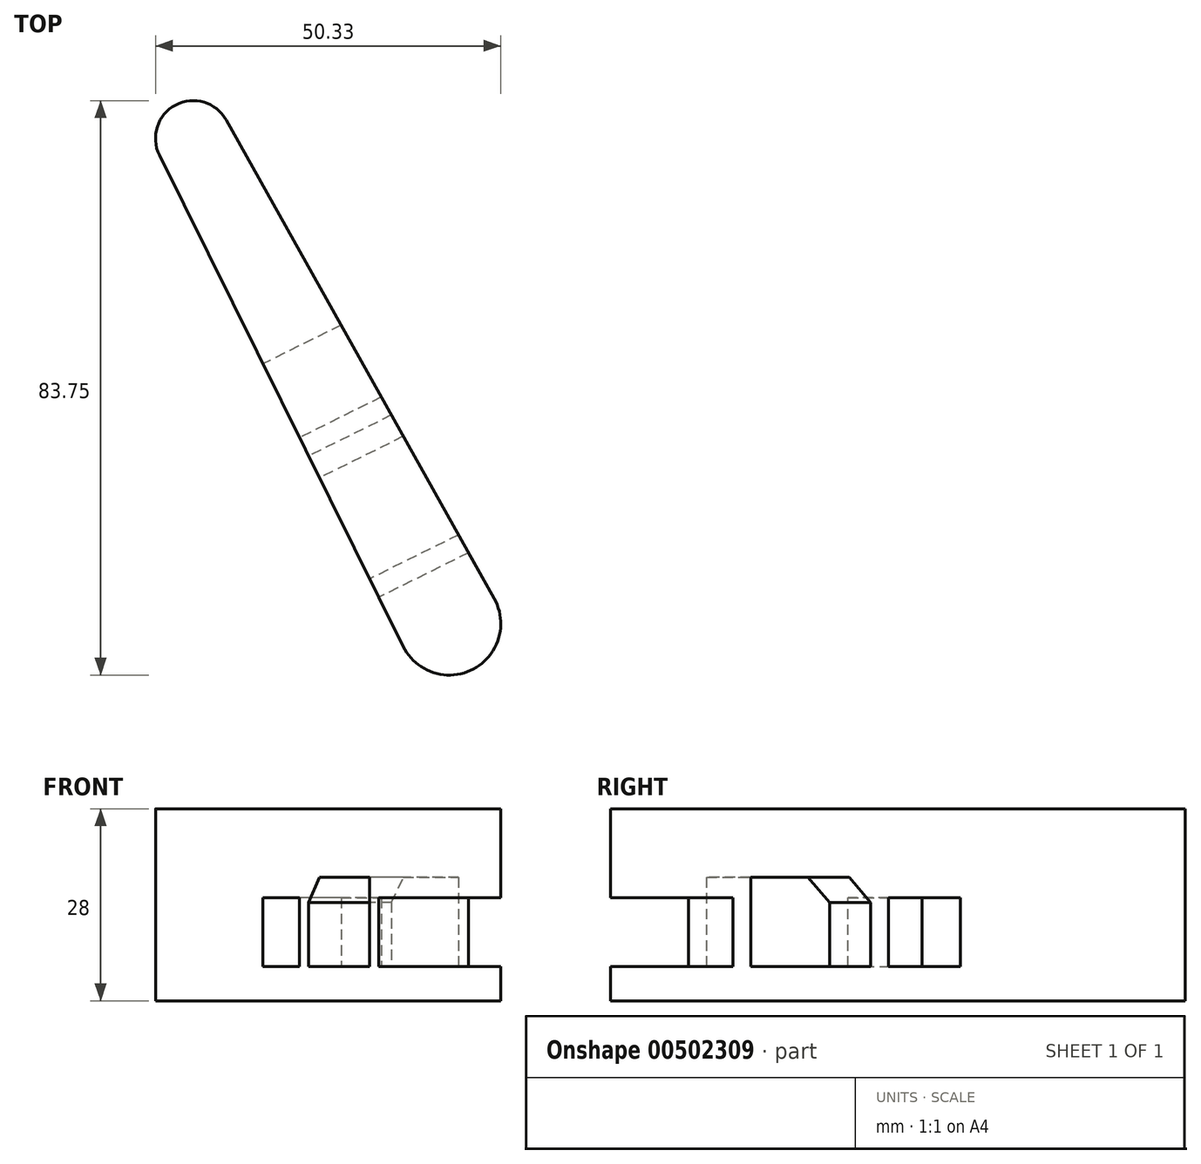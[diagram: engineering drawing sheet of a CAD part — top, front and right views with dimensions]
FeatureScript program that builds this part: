
annotation { "Feature Type Name" : "Feature", "Feature Type Description" : "" }
export const myFeature = defineFeature(function(context is Context, id is Id, definition is map)
    precondition{}
    {
        {
            var Q0;
            Q0=qCreatedBy(makeId("Top.planeOp"),FACE);
            var sketch = newSketch(context, id + "F0", { "sketchPlane" : qUnion([Q0])});
            skCircle(sketch, "E0", {"center": v(-17.98, -33.67) * mm, "radius": 7.5 * mm});
            skLineSegment(sketch, "E1", {"start": v(-17.98, -33.67) * mm, "end": v(-55.31, 37.08) * mm});
            skCircle(sketch, "E2", {"center": v(-55.31, 37.08) * mm, "radius": 5.5 * mm});
            skLineSegment(sketch, "E3", {"start": v(-50.52, 39.8) * mm, "end": v(-11.44, -30) * mm});
            skLineSegment(sketch, "E4", {"start": v(-11.44, -30) * mm, "end": v(-24.7, -37) * mm});
            skLineSegment(sketch, "E5", {"start": v(-24.7, -37) * mm, "end": v(-60.24, 34.64) * mm});
            skSolve(sketch);
        }
        {
            var Q0;
            Q0 = qSketchRegion(id + "F0", true);
            extrude(context, id + "F1", {"entities" : qUnion([Q0]), "depth" : 28 * mm});
        }
        {
            var Q0;
            Q0=makeQuery(id+"F1.opExtrude","SWEPT_FACE",FACE,{"disambiguationData":[OSD([sQuery(id+"F0.wireOp",EDGE,"E5")])]});
            var sketch = newSketch(context, id + "F2", { "sketchPlane" : qUnion([Q0])});
            skLineSegment(sketch, "E6", {"start": v(22.18, 0) * mm, "end": v(22.18, 5) * mm});
            skLineSegment(sketch, "E7.bottom", {"start": v(22.18, 5) * mm, "end": v(14.18, 5) * mm});
            skLineSegment(sketch, "E7.top", {"start": v(22.18, 15) * mm, "end": v(14.18, 15) * mm});
            skLineSegment(sketch, "E7.left", {"start": v(22.18, 5) * mm, "end": v(22.18, 15) * mm});
            skLineSegment(sketch, "E7.right", {"start": v(14.18, 5) * mm, "end": v(14.18, 15) * mm});
            skLineSegment(sketch, "E8.bottom", {"start": v(22.18, 5) * mm, "end": v(34.45, 5) * mm});
            skLineSegment(sketch, "E8.top", {"start": v(22.18, 15) * mm, "end": v(34.45, 15) * mm});
            skLineSegment(sketch, "E8.right", {"start": v(34.45, 5) * mm, "end": v(34.45, 15) * mm});
            skSolve(sketch);
        }
        {
            var Q0;
            Q0 = qSketchRegion(id + "F2", true);
            extrude(context, id + "F3", {"entities" : qUnion([Q0]), "operationType" : NewBodyOperationType.REMOVE, "oppositeDirection" : true, "depth" : 25 * mm});
        }
        {
            var Q0;
            Q0=makeQuery(id+"F1.opExtrude","SWEPT_FACE",FACE,{"disambiguationData":[OSD([sQuery(id+"F0.wireOp",EDGE,"E5")])]});
            var sketch = newSketch(context, id + "F4", { "sketchPlane" : qUnion([Q0])});
            skLineSegment(sketch, "E9", {"start": v(14.18, 5) * mm, "end": v(11.18, 5) * mm});
            skLineSegment(sketch, "E10.bottom", {"start": v(11.18, 5) * mm, "end": v(-8.82, 5) * mm});
            skLineSegment(sketch, "E10.top", {"start": v(11.18, 18) * mm, "end": v(-8.82, 18) * mm});
            skLineSegment(sketch, "E10.left", {"start": v(11.18, 5) * mm, "end": v(11.18, 18) * mm});
            skLineSegment(sketch, "E10.right", {"start": v(-8.82, 5) * mm, "end": v(-8.82, 18) * mm});
            skLineSegment(sketch, "E11", {"start": v(-5.27, 18) * mm, "end": v(-8.82, 14.34) * mm});
            skSolve(sketch);
        }
        {
            var Q0;
            {var subQ1=sQuery(id+"F4.wireOp",EDGE,"E10.bottom");Q0=makeQuery(id+"F4.imprint","IMPRINT",FACE,{"disambiguationData":[TD([[makeQuery(id+"F4.imprint","IMPRINT",EDGE,{"derivedFrom":subQ1}),-1.0]])]});}
            extrude(context, id + "F5", {"entities" : qUnion([Q0]), "operationType" : NewBodyOperationType.REMOVE, "oppositeDirection" : true, "depth" : 25 * mm});
        }
        {
            var Q0;
            Q0=makeQuery(id+"F1.opExtrude","SWEPT_FACE",FACE,{"disambiguationData":[OSD([sQuery(id+"F0.wireOp",EDGE,"E5")])]});
            var sketch = newSketch(context, id + "F6", { "sketchPlane" : qUnion([Q0])});
            skLineSegment(sketch, "E12", {"start": v(-8.82, 5) * mm, "end": v(-11.82, 5) * mm});
            skLineSegment(sketch, "E13.bottom", {"start": v(-11.82, 5) * mm, "end": v(-23.82, 5) * mm});
            skLineSegment(sketch, "E13.top", {"start": v(-11.82, 15) * mm, "end": v(-23.82, 15) * mm});
            skLineSegment(sketch, "E13.left", {"start": v(-11.82, 5) * mm, "end": v(-11.82, 15) * mm});
            skLineSegment(sketch, "E13.right", {"start": v(-23.82, 5) * mm, "end": v(-23.82, 15) * mm});
            skSolve(sketch);
        }
        {
            var Q0;
            Q0 = qSketchRegion(id + "F6", true);
            extrude(context, id + "F7", {"entities" : qUnion([Q0]), "operationType" : NewBodyOperationType.REMOVE, "oppositeDirection" : true, "depth" : 25 * mm});
        }
    });
